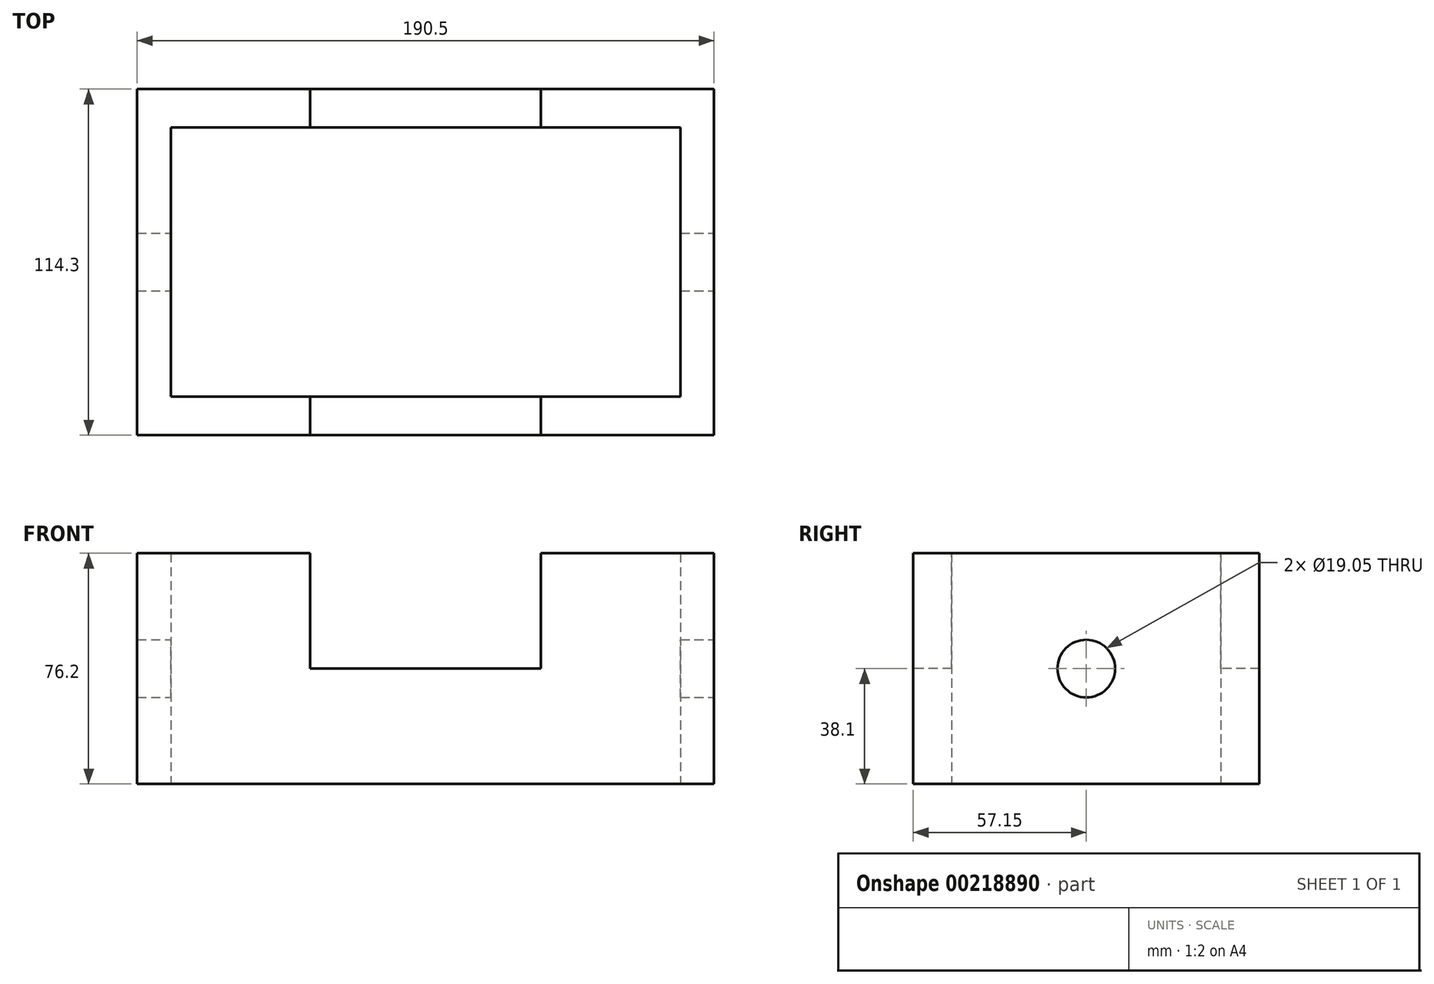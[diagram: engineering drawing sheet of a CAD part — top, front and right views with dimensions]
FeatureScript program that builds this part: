
annotation { "Feature Type Name" : "Feature", "Feature Type Description" : "" }
export const myFeature = defineFeature(function(context is Context, id is Id, definition is map)
    precondition{}
    {
        {
            var Q0;
            Q0=qCreatedBy(makeId("Top.planeOp"),FACE);
            var sketch = newSketch(context, id + "F0", { "sketchPlane" : qUnion([Q0])});
            skLineSegment(sketch, "E0.bottom", {"start": v(95.25, 57.15) * mm, "end": v(-95.25, 57.15) * mm});
            skLineSegment(sketch, "E0.top", {"start": v(95.25, -57.15) * mm, "end": v(-95.25, -57.15) * mm});
            skLineSegment(sketch, "E0.left", {"start": v(95.25, 57.15) * mm, "end": v(95.25, -57.15) * mm});
            skLineSegment(sketch, "E0.right", {"start": v(-95.25, 57.15) * mm, "end": v(-95.25, -57.15) * mm});
            skPoint(sketch, "E0.middle", {"position": v(0, 0) * mm});
            skLineSegment(sketch, "E1.bottom", {"start": v(84.14, 44.45) * mm, "end": v(-84.14, 44.45) * mm});
            skLineSegment(sketch, "E1.top", {"start": v(84.14, -44.45) * mm, "end": v(-84.14, -44.45) * mm});
            skLineSegment(sketch, "E1.left", {"start": v(84.14, 44.45) * mm, "end": v(84.14, -44.45) * mm});
            skLineSegment(sketch, "E1.right", {"start": v(-84.14, 44.45) * mm, "end": v(-84.14, -44.45) * mm});
            skSolve(sketch);
        }
        {
            var Q0;
            Q0 = qSketchRegion(id + "F0", true);
            extrude(context, id + "F1", {"entities" : qUnion([Q0]), "depth" : 76.2 * mm});
        }
        {
            var Q0;
            Q0=makeQuery(id+"F1.opExtrude","SWEPT_FACE",FACE,{"disambiguationData":[OSD([sQuery(id+"F0.wireOp",EDGE,"E0.top")])]});
            var sketch = newSketch(context, id + "F2", { "sketchPlane" : qUnion([Q0])});
            skLineSegment(sketch, "E2.bottom", {"start": v(-38.1, 38.1) * mm, "end": v(38.1, 38.1) * mm});
            skLineSegment(sketch, "E2.top", {"start": v(-38.1, 114.3) * mm, "end": v(38.1, 114.3) * mm});
            skLineSegment(sketch, "E2.left", {"start": v(-38.1, 38.1) * mm, "end": v(-38.1, 114.3) * mm});
            skLineSegment(sketch, "E2.right", {"start": v(38.1, 38.1) * mm, "end": v(38.1, 114.3) * mm});
            skPoint(sketch, "E2.middle", {"position": v(0, 76.2) * mm});
            skSolve(sketch);
        }
        {
            var Q0;
            Q0 = qSketchRegion(id + "F2", true);
            extrude(context, id + "F3", {"entities" : qUnion([Q0]), "operationType" : NewBodyOperationType.REMOVE, "endBound" : BoundingType.SYMMETRIC, "oppositeDirection" : true, "depth" : 381 * mm});
        }
        {
            var Q0;
            Q0=makeQuery(id+"F1.opExtrude","SWEPT_FACE",FACE,{"disambiguationData":[OSD([sQuery(id+"F0.wireOp",EDGE,"E0.left")])]});
            var sketch = newSketch(context, id + "F4", { "sketchPlane" : qUnion([Q0])});
            skCircle(sketch, "E3", {"center": v(0, 38.1) * mm, "radius": 9.53 * mm});
            skPoint(sketch, "E3.centerSnap0", {"position": v(-57.15, 38.1) * mm});
            skPoint(sketch, "E3.centerSnap1", {"position": v(0, 76.2) * mm});
            skSolve(sketch);
        }
        {
            var Q0;
            Q0 = qSketchRegion(id + "F4", true);
            extrude(context, id + "F5", {"entities" : qUnion([Q0]), "operationType" : NewBodyOperationType.REMOVE, "endBound" : BoundingType.SYMMETRIC, "oppositeDirection" : true, "depth" : 381 * mm});
        }
    });
